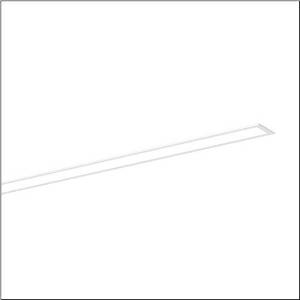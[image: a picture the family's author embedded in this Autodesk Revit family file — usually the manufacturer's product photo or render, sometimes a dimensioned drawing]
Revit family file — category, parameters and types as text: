
# Revit family: silica_r__21_51mx10dc35wb_43eb
name_source: partatom
category: Lighting Fixtures
units: mm (PartAtom-declared; Revit-internal decimal feet)

## family parameters
Cut with Voids When Loaded = No
Host = Face
Light Source = No
Part Type = Normal
Room Calculation Point = No
Round Connector Dimension = Use Diameter
Shared = No

## types (1)
- --- (1 x LED, 6000 lm, 42.6 W, 3000K)
    Apparent Load = 43 VA
    CIE Flux Codes = 48 79 96 100 100
    Color Rendering = 80
    Color Temperature = 3000K
    Default Elevation = 1800 mm
    Description = Silica® 21, office luminaire, primary optical cover: cover, of PMMA, opal, light emission: direct distribution, primary light characteristic: symmetric, installation type: recessed, LED, rated luminous flux: 6.000lm, luminous efficacy: 141lm/W, light colour: 830, colour temperature: 3000K, control gear: DALI 2, with terminal, 3+2-pole, max. 2.5mm², mains connection: 220..240V, AC, 50/60Hz, rated input power: 42.6W, luminaire housing, of aluminium, traffic white (RAL 9016), length: 3.028mm, width: 79mm, height: 53mm, protection rating (complete): IP20, insulation class (complete): insulation class I (protective earthing), certification: CE, ENEC, VDE, permissible operating ambient temperature: 0..+35°C, standard: EN 50419, packaging unit: 1 piece
    Height = 0 mm  [stored 0 ft]
    Lamp = 1 x LED
    Lamp Light Flux = 6000 lm
    Lamp Power = 42.6 W
    Lamp count = 1
    Length = 3027 mm
    Luminous efficacy = 141 lm/W
    Manufacturer = Siteco
    ModVariant = No
    Model = 51MX10DC35WB
    Mounting Place = Ceiling
    Mounting Type = Recessed
    Number of Poles = 1
    OnlyDefault = Yes
    Power Factor = 1
    Product Name = Silica® 21
    Product group = office luminaire | ceiling recessed
    ProductGroupID = 401
    Protection Class = Protection class I
    Protection Degree = IP 20
    RLX_Detail_Level = 1
    RLX_Emergency_Light_Flux = 0 lm
    RLX_Emergency_Type = 0
    RLX_Emergency_Type_DB = No
    RlxData = <blob elided: 21205 chars, md5=6fad02f0>
    Socket = socket
    Standby Power = 0 W
    System Light Flux = 6000 lm
    System Power = 43 W
    Type Comments = factory setting: luminous flux: 100 % | dim-lin: 254 | 233 mA
    Type Image = l_1335891.jpg
    URL = http://relux.com
    VarID = @adj_117596
    Voltage = 0 V
    Weight = 0.00 kg
    Width = 79 mm

note: [stored X ft] marks values corroborated as IEEE doubles in the binary element streams (Revit-internal decimal feet)

## geometry (parser evidence)
native form markers: Blend x4, Sweep x11
no freeform markers — native parametric forms only
